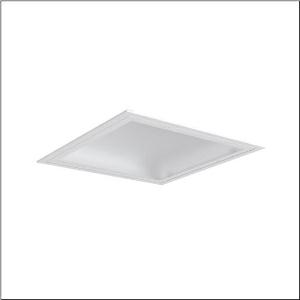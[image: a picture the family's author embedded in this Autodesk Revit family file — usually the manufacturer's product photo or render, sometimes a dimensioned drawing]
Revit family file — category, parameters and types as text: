
# Revit family: mira_r__21_51fr427a462a_66f5
name_source: partatom
category: Lighting Fixtures
units: mm (PartAtom-declared; Revit-internal decimal feet)

## family parameters
Cut with Voids When Loaded = No
Host = Face
Light Source = No
Part Type = Normal
Room Calculation Point = No
Round Connector Dimension = Use Diameter
Shared = No

## types (1)
- Mira® 21 (1 x LED, 6420 lm, 53 W, 4000K)
    Apparent Load = 53 VA
    CIE Flux Codes = 50 81 97 100 100
    Color Rendering = 80
    Color Temperature = 4000K
    Default Elevation = 1800 mm
    Description = Mira® 21, clean room luminaire, primary light control with reflector, primary optical cover: cover, of PC, light emission: direct distribution, primary light characteristic: symmetric, installation type: recessed, LED, rated luminous flux: 6.420lm, luminous efficacy: 121lm/W, light colour: 840, colour temperature: 4000K, control gear: ECG, with terminal, 3-pole, max. 2.5mm², mains connection: 230V, AC, 50/60Hz, rated input power: 53W, luminaire housing, of sheet steel, coated, pure white (RAL 9010), with concealed spring brackets, module: M625, length: 623mm, width: 623mm, height: 115mm, protection rating (complete): IP54, insulation class (complete): insulation class I (protective earthing), certification: CE, UKCA, permissible operating ambient temperature: -5..+40°C, standard: EN 50419, packaging unit: 1 piece
    Height = 0 mm  [stored 0 ft]
    Lamp = 1 x LED
    Lamp Light Flux = 6420 lm
    Lamp Power = 53 W
    Lamp count = 1
    Length = 625 mm
    Luminous efficacy = 121 lm/W
    Manufacturer = Siteco
    ModVariant = No
    Model = 51FR427A462A
    Mounting Place = Ceiling
    Mounting Type = Recessed
    Number of Poles = 1
    OnlyDefault = Yes
    Power Factor = 1
    Product Name = Mira® 21
    Product group = clean room luminaire
    ProductGroupID = 402
    Protection Class = Protection class I
    Protection Degree = IP 54
    RLX_Detail_Level = 1
    RLX_Emergency_Light_Flux = 0 lm
    RLX_Emergency_Type = 0
    RLX_Emergency_Type_DB = No
    RlxData = <blob elided: 13377 chars, md5=597f0c51>
    Socket = socket
    Standby Power = 0 W
    System Light Flux = 6420 lm
    System Power = 53 W
    Type Comments = Product without accessories
    Type Image = l_1007109.jpg
    URL = http://relux.com
    VarID = ---
    Voltage = 0 V
    Weight = 0.00 kg
    Width = 625 mm

note: [stored X ft] marks values corroborated as IEEE doubles in the binary element streams (Revit-internal decimal feet)

## geometry (parser evidence)
native form markers: Sweep x10
no freeform markers — native parametric forms only
